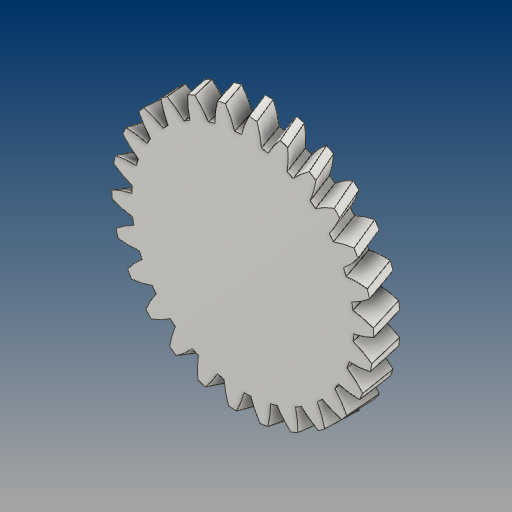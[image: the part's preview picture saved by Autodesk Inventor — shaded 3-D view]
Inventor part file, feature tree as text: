
AUTODESK INVENTOR PART (.ipt)
format: ipt  version: 2021 (Build 250183000, 183)  size: 494,080 bytes
history: native  units: mm (DEFAULTED — no unit token found)
features: plane x3, other x3, sketch x2, extrude x1
ambient origin geometry x8: Origin, YZ Plane, XZ Plane, XY Plane, X Axis, Y Axis, Z Axis, Center Point
bodies: Solid1 (feature_tree)
feature tree (9):
  extrude  "Extrusion1"  Depth=15.0mm TaperAngle=0.0deg
  plane  "Work Plane2"
  plane  "Work Plane8"
  plane  "Work Plane9"
  other  "Spur Gear"
  sketch  "Sketch1"  dims[d0=148.34311mm d1=15.0mm d2=0.0mm]
  sketch  "Sketch2"  dims[d3=138.34311mm d4=10.0mm d5=0.0mm d16=70.0mm d17=0.0mm d34=1.208305mm d39=0.0mm d41=0.0mm d43=70.0mm d46=70.0mm d47=0.0mm d48=0.0mm]
  other  "Srf1"
  other  "Pitch Diameter"
